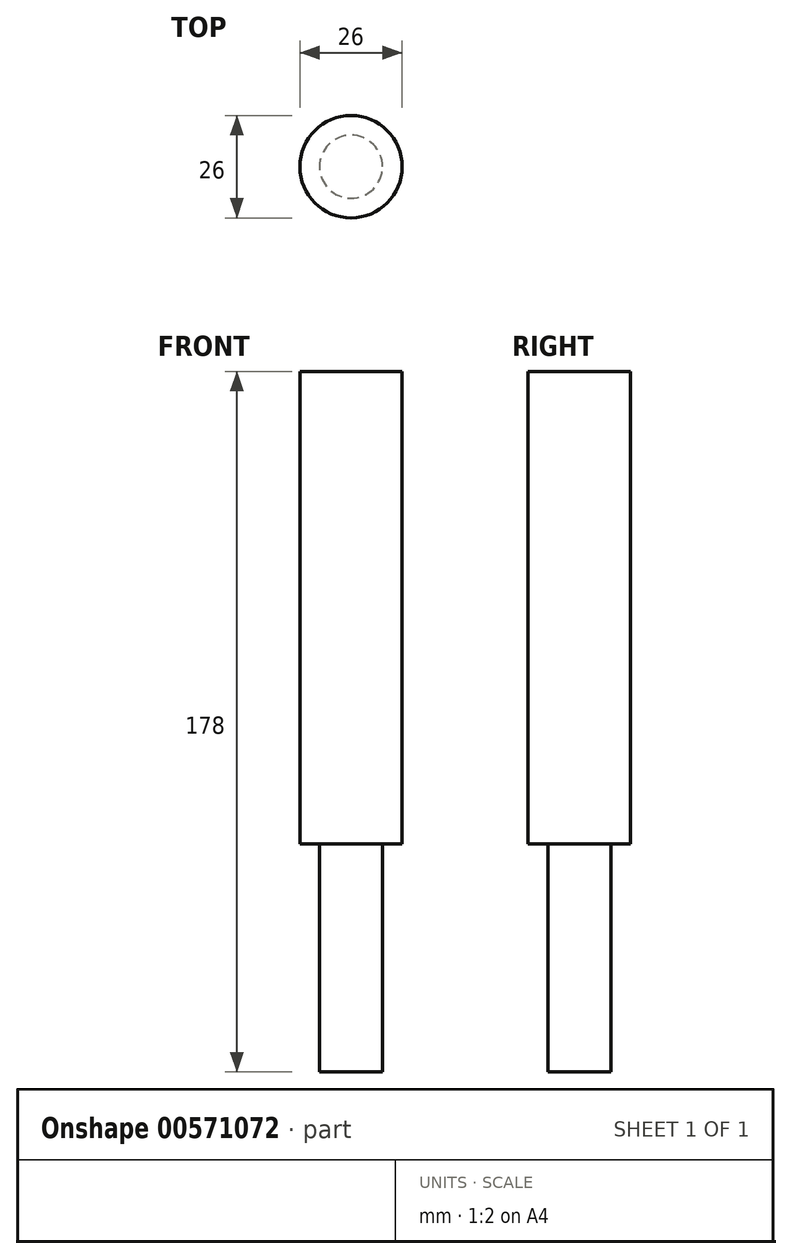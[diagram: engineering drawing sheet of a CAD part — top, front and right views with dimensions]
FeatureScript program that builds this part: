
annotation { "Feature Type Name" : "Feature", "Feature Type Description" : "" }
export const myFeature = defineFeature(function(context is Context, id is Id, definition is map)
    precondition{}
    {
        {
            var Q0;
            Q0=qCreatedBy(makeId("Top.planeOp"),FACE);
            var sketch = newSketch(context, id + "F0", { "sketchPlane" : qUnion([Q0])});
            skCircle(sketch, "E0", {"center": v(0, 0) * mm, "radius": 13 * mm});
            skCircle(sketch, "E1", {"center": v(0, 0) * mm, "radius": 8 * mm});
            skSolve(sketch);
        }
        {
            var Q0;
            Q0 = qSketchRegion(id + "F0", true);
            var Q1;
            Q1=makeQuery(id+"F0.imprint","IMPRINT",FACE,{"disambiguationData":[TD([[makeQuery(id+"F0.imprint","IMPRINT",EDGE,{"derivedFrom":sQuery(id+"F0.wireOp",EDGE,"E0")}),1.0]])]});
            var Q2;
            Q2=makeQuery(id+"F0.imprint","IMPRINT",FACE,{"disambiguationData":[TD([[makeQuery(id+"F0.imprint","IMPRINT",EDGE,{"derivedFrom":sQuery(id+"F0.wireOp",EDGE,"E1")}),1.0]])]});
            extrude(context, id + "F1", {"entities" : qUnion([Q0, Q1, Q2]), "depth" : 178 * mm, "offsetDistance" : 25 * mm});
        }
        {
            var Q0;
            Q0=makeQuery(id+"F0.imprint","IMPRINT",FACE,{"disambiguationData":[TD([[makeQuery(id+"F0.imprint","IMPRINT",EDGE,{"derivedFrom":sQuery(id+"F0.wireOp",EDGE,"E0")}),1.0]])]});
            extrude(context, id + "F2", {"entities" : qUnion([Q0]), "operationType" : NewBodyOperationType.REMOVE, "depth" : 58 * mm, "offsetDistance" : 25 * mm});
        }
    });
